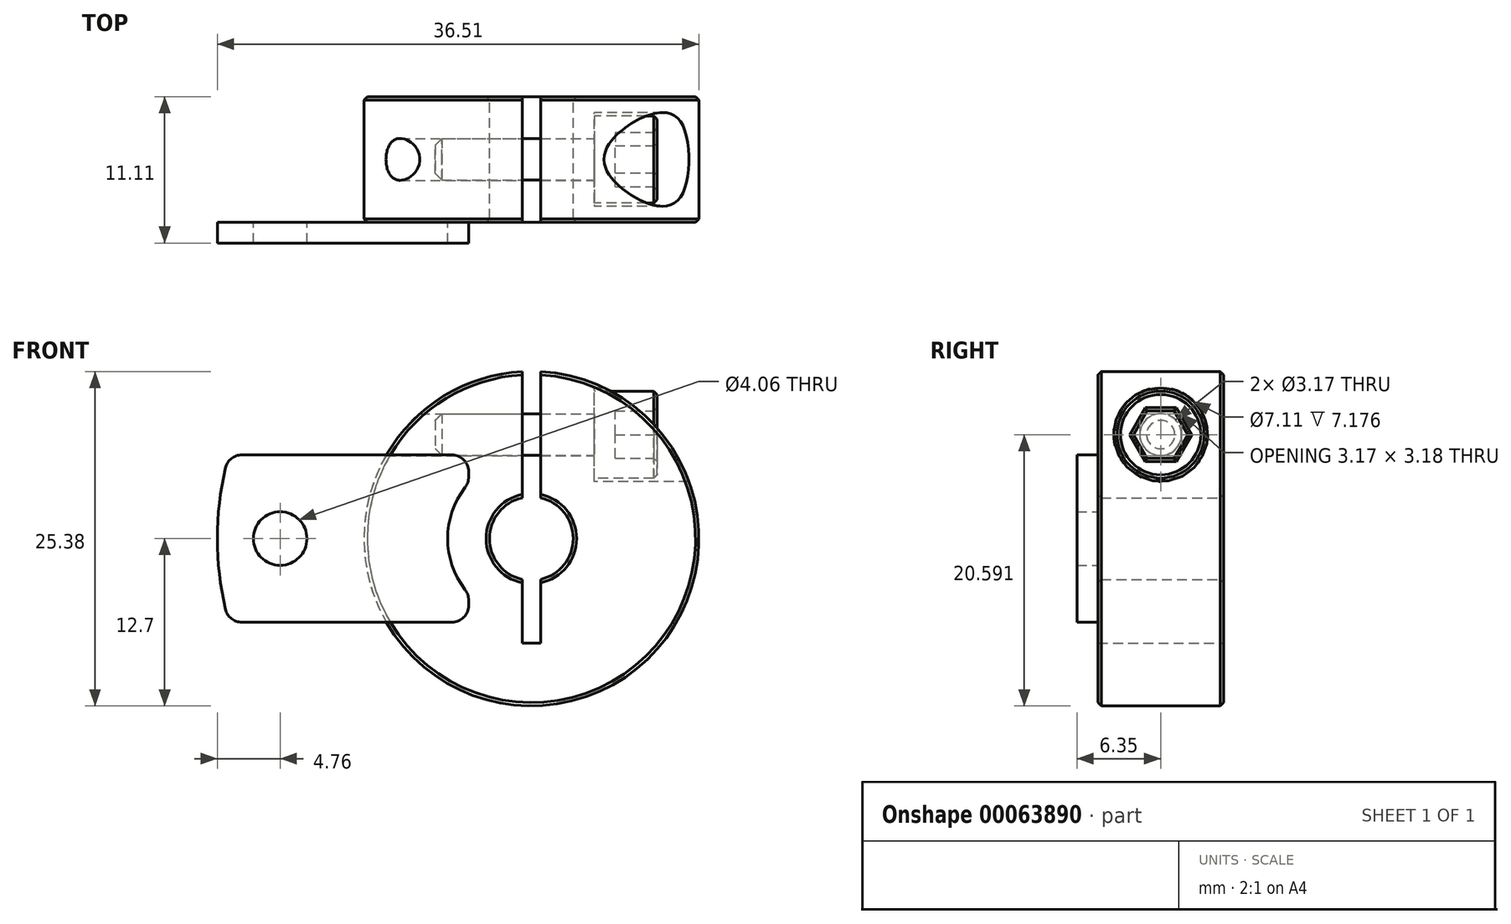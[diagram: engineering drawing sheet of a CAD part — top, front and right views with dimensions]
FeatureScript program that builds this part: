
annotation { "Feature Type Name" : "Feature", "Feature Type Description" : "" }
export const myFeature = defineFeature(function(context is Context, id is Id, definition is map)
    precondition{}
    {
        {
            var Q0;
            Q0=qCreatedBy(makeId("Front.planeOp"),FACE);
            var sketch = newSketch(context, id + "F0", { "sketchPlane" : qUnion([Q0])});
            skArc(sketch, "E0", {"start": v(-0.7, 12.68) * mm, "mid": v(0, -12.7) * mm, "end": v(0.7, 12.68) * mm});
            skArc(sketch, "E1", {"start": v(-0.7, 3.1) * mm, "mid": v(-3.18, 0) * mm, "end": v(-0.7, -3.1) * mm});
            skLineSegment(sketch, "E2.bottom", {"start": v(0.7, -7.94) * mm, "end": v(-0.7, -7.94) * mm});
            skLineSegment(sketch, "E2.left", {"start": v(0.7, -7.94) * mm, "end": v(0.7, -3.1) * mm});
            skLineSegment(sketch, "E2.right", {"start": v(-0.7, -7.94) * mm, "end": v(-0.7, -3.1) * mm});
            skLineSegment(sketch, "E3", {"start": v(0, 0) * mm, "end": v(0.7, 0) * mm, "construction": true});
            skLineSegment(sketch, "E4", {"start": v(0, 0) * mm, "end": v(-0.7, 0) * mm, "construction": true});
            skLineSegment(sketch, "E5.trimOffspring", {"start": v(-0.7, 3.1) * mm, "end": v(-0.7, 12.68) * mm});
            skLineSegment(sketch, "E6.trimOffspring", {"start": v(0.7, 3.1) * mm, "end": v(0.7, 12.68) * mm});
            skArc(sketch, "E7.trimOffspring", {"start": v(0.7, -3.1) * mm, "mid": v(3.18, 0) * mm, "end": v(0.7, 3.1) * mm});
            skLineSegment(sketch, "E8", {"start": v(0.7, 3.1) * mm, "end": v(0.7, -3.1) * mm, "construction": true});
            skLineSegment(sketch, "E9", {"start": v(-0.7, -3.1) * mm, "end": v(-0.7, 3.1) * mm, "construction": true});
            skSolve(sketch);
        }
        {
            var Q0;
            Q0 = qSketchRegion(id + "F0", true);
            extrude(context, id + "F1", {"entities" : qUnion([Q0]), "endBound" : BoundingType.SYMMETRIC, "depth" : 9.52 * mm});
        }
        {
            var Q0;
            Q0=makeQuery(id+"F1.opExtrude","CAP_EDGE",EDGE,{"disambiguationData":[OSD([sQuery(id+"F0.wireOp",EDGE,"E0")])],"isStart":false});
            var Q1;
            Q1=makeQuery(id+"F1.opExtrude","CAP_EDGE",EDGE,{"disambiguationData":[OSD([sQuery(id+"F0.wireOp",EDGE,"E1")])],"isStart":false});
            var Q2;
            Q2=makeQuery(id+"F1.opExtrude","CAP_EDGE",EDGE,{"disambiguationData":[OSD([sQuery(id+"F0.wireOp",EDGE,"E0")])],"isStart":true});
            var Q3;
            Q3=makeQuery(id+"F1.opExtrude","CAP_EDGE",EDGE,{"disambiguationData":[OSD([sQuery(id+"F0.wireOp",EDGE,"E1")])],"isStart":true});
            var Q4;
            Q4=makeQuery(id+"F1.opExtrude","CAP_EDGE",EDGE,{"disambiguationData":[OSD([sQuery(id+"F0.wireOp",EDGE,"E7.trimOffspring")])],"isStart":true});
            var Q5;
            Q5=makeQuery(id+"F1.opExtrude","CAP_EDGE",EDGE,{"disambiguationData":[OSD([sQuery(id+"F0.wireOp",EDGE,"E7.trimOffspring")])],"isStart":false});
            chamfer(context, id + "F2", {"entities" : qUnion([Q0, Q1, Q2, Q3, Q4, Q5]), "width" : 0.25 * mm, "tangentPropagation" : true});
        }
        {
            var Q0;
            Q0=makeQuery(id+"F1.opExtrude","CAP_FACE",FACE,{"disambiguationData":[OSD([sQuery(id+"F0.wireOp",EDGE,"E0"),sQuery(id+"F0.wireOp",EDGE,"E1"),sQuery(id+"F0.wireOp",EDGE,"E2.bottom"),sQuery(id+"F0.wireOp",EDGE,"E2.left"),sQuery(id+"F0.wireOp",EDGE,"E2.right"),sQuery(id+"F0.wireOp",EDGE,"E5.trimOffspring"),sQuery(id+"F0.wireOp",EDGE,"E6.trimOffspring"),sQuery(id+"F0.wireOp",EDGE,"E7.trimOffspring")])],"isStart":false});
            var sketch = newSketch(context, id + "F3", { "sketchPlane" : qUnion([Q0])});
            skLineSegment(sketch, "E10.bottom", {"start": v(-21.96, 6.35) * mm, "end": v(-6.03, 6.35) * mm});
            skLineSegment(sketch, "E10.top", {"start": v(-21.96, -6.35) * mm, "end": v(-6.03, -6.35) * mm});
            skLineSegment(sketch, "E10.right", {"start": v(-4.76, 5.08) * mm, "end": v(-4.76, 4.66) * mm});
            skLineSegment(sketch, "E11", {"start": v(0, 0) * mm, "end": v(-23.81, 0) * mm, "construction": true});
            skArc(sketch, "E12", {"start": v(-5.03, 3.88) * mm, "mid": v(-6.35, 0) * mm, "end": v(-5.03, -3.88) * mm});
            skLineSegment(sketch, "E13.trimOffspring", {"start": v(-4.76, -4.66) * mm, "end": v(-4.76, -5.08) * mm});
            skArc(sketch, "E14", {"start": v(-23.2, 5.37) * mm, "mid": v(-23.81, 0) * mm, "end": v(-23.2, -5.37) * mm});
            skPoint(sketch, "E15.visualSharp", {"position": v(-4.76, 6.35) * mm});
            skArc(sketch, "E15.filletArc", {"start": v(-4.76, 5.08) * mm, "mid": v(-5.13, 5.98) * mm, "end": v(-6.03, 6.35) * mm});
            skPoint(sketch, "E16.visualSharp", {"position": v(-4.76, 4.2) * mm});
            skArc(sketch, "E16.filletArc", {"start": v(-5.03, 3.88) * mm, "mid": v(-4.83, 4.25) * mm, "end": v(-4.76, 4.66) * mm});
            skPoint(sketch, "E17.visualSharp", {"position": v(-4.76, -4.2) * mm});
            skArc(sketch, "E17.filletArc", {"start": v(-4.76, -4.66) * mm, "mid": v(-4.83, -4.25) * mm, "end": v(-5.03, -3.88) * mm});
            skPoint(sketch, "E18.visualSharp", {"position": v(-4.76, -6.35) * mm});
            skArc(sketch, "E18.filletArc", {"start": v(-6.03, -6.35) * mm, "mid": v(-5.13, -5.98) * mm, "end": v(-4.76, -5.08) * mm});
            skPoint(sketch, "E19.visualSharp", {"position": v(-22.95, 6.35) * mm});
            skArc(sketch, "E19.filletArc", {"start": v(-21.96, 6.35) * mm, "mid": v(-22.75, 6.07) * mm, "end": v(-23.2, 5.37) * mm});
            skPoint(sketch, "E20.visualSharp", {"position": v(-22.95, -6.35) * mm});
            skArc(sketch, "E20.filletArc", {"start": v(-23.2, -5.37) * mm, "mid": v(-22.75, -6.07) * mm, "end": v(-21.96, -6.35) * mm});
            skCircle(sketch, "E21", {"center": v(-19.05, 0) * mm, "radius": 2.03 * mm});
            skSolve(sketch);
        }
        {
            var Q0;
            Q0=makeQuery(id+"F3.imprint","IMPRINT",FACE,{"disambiguationData":[TD([[makeQuery(id+"F3.imprint","IMPRINT",EDGE,{"derivedFrom":sQuery(id+"F3.wireOp",EDGE,"E14")}),1.0]])]});
            var Q1;
            Q1=makeQuery(id+"F3.imprint","IMPRINT",FACE,{"disambiguationData":[TD([[makeQuery(id+"F3.imprint","IMPRINT",EDGE,{"derivedFrom":sQuery(id+"F3.wireOp",EDGE,"E10.right")}),-1.0]])]});
            extrude(context, id + "F4", {"entities" : qUnion([Q0, Q1]), "depth" : 1.59 * mm});
        }
        {
            var Q0;
            Q0=qCreatedBy(makeId("Right.planeOp"),FACE);
            cPlane(context, id + "F5", {"entities" : qUnion([Q0]), "cplaneType" : CPlaneType.OFFSET, "offset" : 4.76 * mm, "width" : 152.4 * mm, "height" : 152.4 * mm});
        }
        {
            var Q0;
            Q0=qCreatedBy(id+"F5.planeOp",FACE);
            var sketch = newSketch(context, id + "F6", { "sketchPlane" : qUnion([Q0])});
            skCircle(sketch, "E22", {"center": v(0, 7.9) * mm, "radius": 3.56 * mm});
            skLineSegment(sketch, "E23.0", {"start": v(-4.5, 12.68) * mm, "end": v(4.5, 12.68) * mm, "construction": true});
            skLineSegment(sketch, "E23.1", {"start": v(-4.5, 3.1) * mm, "end": v(4.5, 3.1) * mm, "construction": true});
            skLineSegment(sketch, "E23.2", {"start": v(4.76, 3.36) * mm, "end": v(4.76, 12.43) * mm, "construction": true});
            skLineSegment(sketch, "E23.3", {"start": v(-4.76, 3.36) * mm, "end": v(-4.76, 12.43) * mm, "construction": true});
            skLineSegment(sketch, "E24", {"start": v(-4.76, 7.9) * mm, "end": v(4.76, 7.9) * mm, "construction": true});
            skLineSegment(sketch, "E25", {"start": v(0, 12.68) * mm, "end": v(0, 3.1) * mm, "construction": true});
            skSolve(sketch);
        }
        {
            var Q0;
            Q0 = qSketchRegion(id + "F6", true);
            extrude(context, id + "F7", {"entities" : qUnion([Q0]), "operationType" : NewBodyOperationType.REMOVE, "depth" : 25.4 * mm});
        }
        {
            var Q0;
            Q0=makeQuery(id+"F7.boolean.opBoolean","COPY",FACE,{"derivedFrom":makeQuery(id+"F7.opExtrude","CAP_FACE",FACE,{"disambiguationData":[OSD([sQuery(id+"F6.wireOp",EDGE,"E22")])],"isStart":true})});
            var sketch = newSketch(context, id + "F8", { "sketchPlane" : qUnion([Q0])});
            skCircle(sketch, "E26", {"center": v(0, 7.9) * mm, "radius": 1.59 * mm});
            skSolve(sketch);
        }
        {
            var Q0;
            Q0 = qSketchRegion(id + "F8", true);
            extrude(context, id + "F9", {"entities" : qUnion([Q0]), "operationType" : NewBodyOperationType.REMOVE, "oppositeDirection" : true, "depth" : 25.4 * mm});
        }
        {
            var Q0;
            Q0=makeQuery(id+"F7.boolean.opBoolean","COPY",FACE,{"derivedFrom":makeQuery(id+"F7.opExtrude","CAP_FACE",FACE,{"disambiguationData":[OSD([sQuery(id+"F6.wireOp",EDGE,"E22")])],"isStart":true})});
            var sketch = newSketch(context, id + "F10", { "sketchPlane" : qUnion([Q0])});
            skCircle(sketch, "E27", {"center": v(0, 7.9) * mm, "radius": 3.3 * mm});
            skSolve(sketch);
        }
        {
            var Q0;
            Q0 = qSketchRegion(id + "F10", true);
            extrude(context, id + "F11", {"entities" : qUnion([Q0]), "depth" : 4.76 * mm});
        }
        {
            var Q0;
            Q0=makeQuery(id+"F11.opExtrude","CAP_FACE",FACE,{"disambiguationData":[OSD([sQuery(id+"F10.wireOp",EDGE,"E27")])],"isStart":true});
            var sketch = newSketch(context, id + "F12", { "sketchPlane" : qUnion([Q0])});
            skCircle(sketch, "E28", {"center": v(0, 7.9) * mm, "radius": 1.58 * mm});
            skSolve(sketch);
        }
        {
            var Q0;
            Q0 = qSketchRegion(id + "F12", true);
            extrude(context, id + "F13", {"entities" : qUnion([Q0]), "operationType" : NewBodyOperationType.ADD, "depth" : 12.06 * mm});
        }
        {
            var Q0;
            Q0=makeQuery(id+"F13.opExtrude","CAP_FACE",FACE,{"disambiguationData":[OSD([sQuery(id+"F12.wireOp",EDGE,"E28")])],"isStart":false});
            chamfer(context, id + "F14", {"entities" : qUnion([Q0]), "width" : 0.5 * mm, "tangentPropagation" : true});
        }
        {
            var Q0;
            Q0=makeQuery(id+"F11.opExtrude","CAP_FACE",FACE,{"disambiguationData":[OSD([sQuery(id+"F10.wireOp",EDGE,"E27")])],"isStart":false});
            var sketch = newSketch(context, id + "F15", { "sketchPlane" : qUnion([Q0])});
            skCircle(sketch, "E29.cCircle", {"center": v(0, 7.9) * mm, "radius": 1.79 * mm, "construction": true});
            skLineSegment(sketch, "E29.0", {"start": v(-1.03, 9.68) * mm, "end": v(1.03, 9.68) * mm});
            skLineSegment(sketch, "E29.1", {"start": v(1.03, 9.68) * mm, "end": v(2.06, 7.9) * mm});
            skLineSegment(sketch, "E29.2", {"start": v(2.06, 7.9) * mm, "end": v(1.03, 6.1) * mm});
            skLineSegment(sketch, "E29.3", {"start": v(1.03, 6.1) * mm, "end": v(-1.03, 6.1) * mm});
            skLineSegment(sketch, "E29.4", {"start": v(-1.03, 6.1) * mm, "end": v(-2.06, 7.9) * mm});
            skLineSegment(sketch, "E29.5", {"start": v(-2.06, 7.9) * mm, "end": v(-1.03, 9.68) * mm});
            skPoint(sketch, "E29.0.midPoint", {"position": v(0, 9.68) * mm});
            skSolve(sketch);
        }
        {
            var Q0;
            Q0 = qSketchRegion(id + "F15", true);
            extrude(context, id + "F16", {"entities" : qUnion([Q0]), "operationType" : NewBodyOperationType.REMOVE, "oppositeDirection" : true, "depth" : 3.17 * mm});
        }
        {
            var Q0;
            Q0=makeQuery(id+"F11.opExtrude","CAP_FACE",FACE,{"disambiguationData":[OSD([sQuery(id+"F10.wireOp",EDGE,"E27")])],"isStart":false});
            chamfer(context, id + "F17", {"entities" : qUnion([Q0]), "width" : 0.25 * mm, "tangentPropagation" : true});
        }
    });
